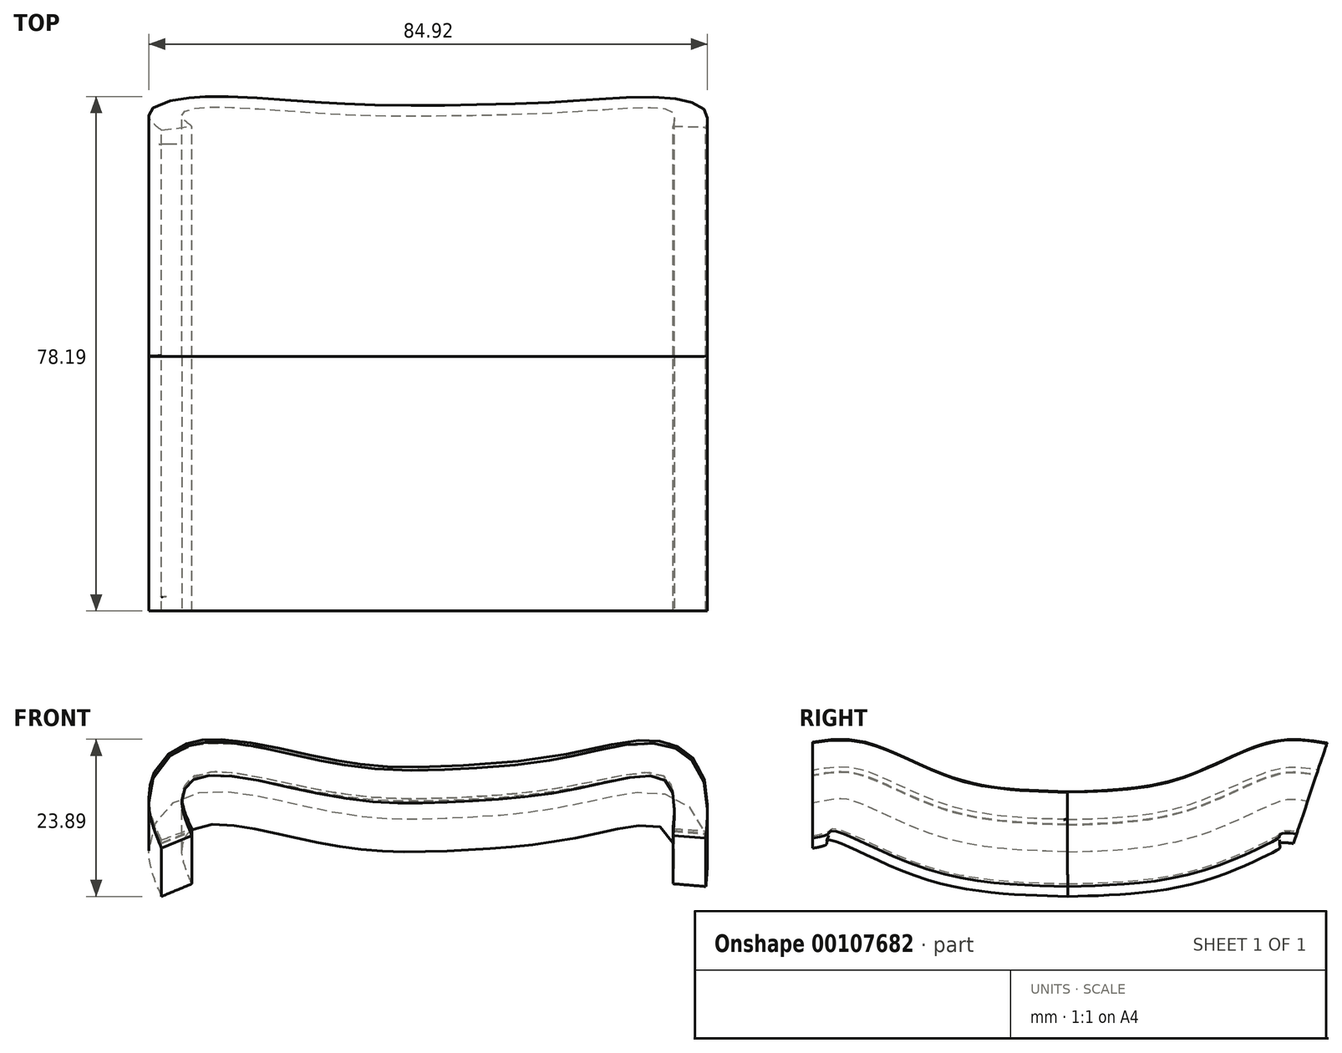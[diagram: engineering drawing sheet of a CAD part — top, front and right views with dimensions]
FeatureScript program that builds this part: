
annotation { "Feature Type Name" : "Feature", "Feature Type Description" : "" }
export const myFeature = defineFeature(function(context is Context, id is Id, definition is map)
    precondition{}
    {
        {
            var Q0;
            Q0=qCreatedBy(makeId("Front.planeOp"),FACE);
            var sketch = newSketch(context, id + "F0", { "sketchPlane" : qUnion([Q0])});
            skFitSpline(sketch, "E0", {"points": [v(-66.72, 0) * mm, v(-68.22, 5.67) * mm, v(-65.23, 8.96) * mm, v(-45.53, 5.97) * mm, v(-27.32, 5.08) * mm, v(-7.91, 7.17) * mm, v(5.22, 8.36) * mm, v(6.42, 0) * mm], "startDerivative": vector(-25.03, 59.24) * mm, "endDerivative": vector(-7.3, -87.83) * mm});
            skFitSpline(sketch, "E1.0", {"points": [v(-71.33, -1.95) * mm, v(-71.6, -1.33) * mm, v(-72.02, -0.32) * mm, v(-72.57, 1.21) * mm, v(-72.93, 2.48) * mm, v(-73.2, 3.89) * mm, v(-73.27, 5.2) * mm, v(-73.19, 6.35) * mm, v(-72.99, 7.52) * mm, v(-72.5, 9) * mm, v(-71.5, 10.7) * mm, v(-70.3, 11.9) * mm, v(-69.19, 12.68) * mm, v(-68.3, 13.17) * mm, v(-67.5, 13.5) * mm, v(-66.87, 13.7) * mm, v(-66.38, 13.83) * mm, v(-65.9, 13.93) * mm, v(-65.26, 14.04) * mm, v(-64.48, 14.13) * mm, v(-63.56, 14.18) * mm, v(-62.35, 14.18) * mm, v(-60.85, 14.08) * mm, v(-59.02, 13.86) * mm, v(-57.17, 13.55) * mm, v(-54.65, 13.06) * mm, v(-52.1, 12.5) * mm, v(-49.58, 11.92) * mm, v(-47.73, 11.5) * mm, v(-46.23, 11.2) * mm, v(-45.08, 10.97) * mm, v(-43.96, 10.77) * mm, v(-42.6, 10.55) * mm, v(-40.5, 10.27) * mm, v(-37.99, 10.04) * mm, v(-35.06, 9.92) * mm, v(-32.14, 9.91) * mm, v(-29.66, 9.98) * mm, v(-27.61, 10.07) * mm, v(-25.53, 10.16) * mm, v(-22.9, 10.3) * mm, v(-19.7, 10.54) * mm, v(-16.5, 10.86) * mm, v(-13.82, 11.2) * mm, v(-11.68, 11.54) * mm, v(-10.34, 11.78) * mm, v(-9.28, 11.99) * mm, v(-8.21, 12.2) * mm, v(-6.85, 12.51) * mm, v(-5.17, 12.9) * mm, v(-3.49, 13.27) * mm, v(-1.8, 13.6) * mm, v(-0.1, 13.88) * mm, v(1.62, 14.05) * mm, v(3.12, 14.06) * mm, v(4.4, 13.92) * mm, v(5.4, 13.72) * mm, v(6.46, 13.38) * mm, v(7.36, 12.94) * mm, v(8.08, 12.48) * mm, v(8.77, 11.94) * mm, v(9.51, 11.18) * mm, v(10.2, 10.2) * mm, v(10.88, 8.9) * mm, v(11.35, 7.34) * mm, v(11.6, 5.62) * mm, v(11.65, 4.01) * mm, v(11.61, 2.47) * mm, v(11.52, 0.99) * mm, v(11.44, 0.04) * mm, v(11.4, -0.41) * mm]});
            skLineSegment(sketch, "E2", {"start": v(-71.33, -1.95) * mm, "end": v(-66.72, 0) * mm});
            skLineSegment(sketch, "E3", {"start": v(6.42, 0) * mm, "end": v(11.4, -0.41) * mm});
            skSolve(sketch);
        }
        {
            var Q0;
            Q0=qCreatedBy(makeId("Right.planeOp"),FACE);
            var sketch = newSketch(context, id + "F1", { "sketchPlane" : qUnion([Q0])});
            skFitSpline(sketch, "E4", {"points": [v(0, 11.74) * mm, v(7.36, 11.84) * mm, v(20.98, 6.35) * mm, v(38.7, 4.24) * mm], "startDerivative": vector(27.57, 4.48) * mm, "endDerivative": vector(46.4, -1.24) * mm});
            skFitSpline(sketch, "E5.MirrorCS", {"points": [v(77.42, 11.74) * mm, v(70.06, 11.84) * mm, v(56.44, 6.35) * mm, v(38.7, 4.24) * mm], "startDerivative": vector(-27.57, 4.48) * mm, "endDerivative": vector(-46.4, -1.24) * mm});
            skSolve(sketch);
        }
        {
            var Q0;
            Q0=makeQuery(id+"F0.imprint","IMPRINT",FACE,{"disambiguationData":[TD([[makeQuery(id+"F0.imprint","IMPRINT",EDGE,{"derivedFrom":sQuery(id+"F0.wireOp",EDGE,"E0")}),1.0]])]});
            var Q1;
            Q1=sQuery(id+"F1.wireOp",EDGE,"E4");
            var Q2;
            Q2=sQuery(id+"F1.wireOp",EDGE,"E5.MirrorCS");
            sweep(context, id + "F2", {"profiles" : qUnion([Q0]), "path" : qUnion([Q1, Q2])});
        }
    });
